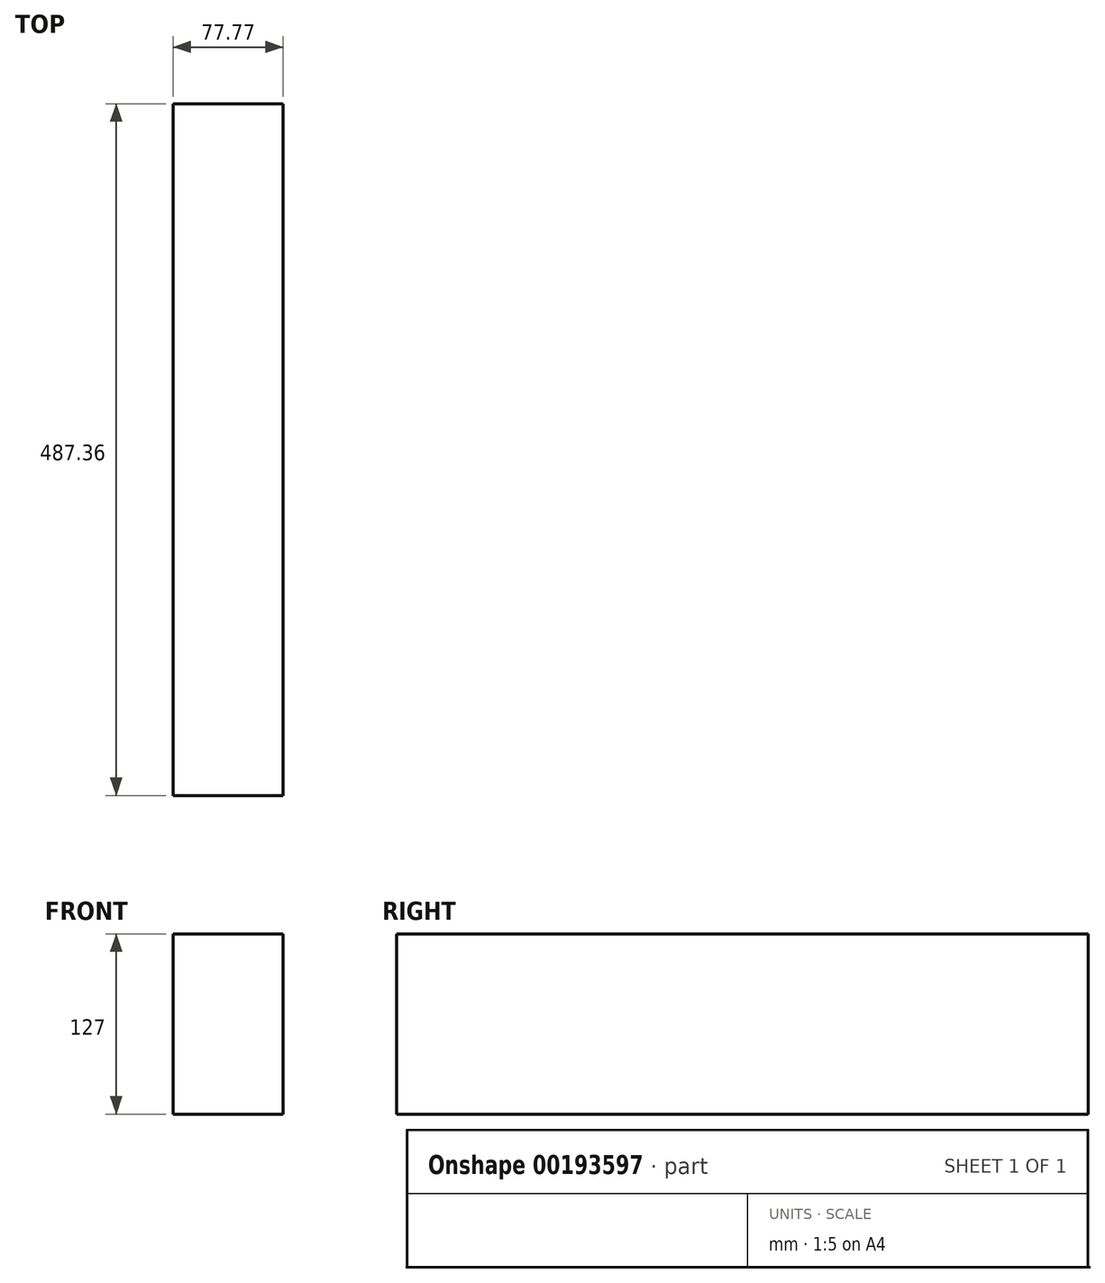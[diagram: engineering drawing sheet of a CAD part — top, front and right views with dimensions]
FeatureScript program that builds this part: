
annotation { "Feature Type Name" : "Feature", "Feature Type Description" : "" }
export const myFeature = defineFeature(function(context is Context, id is Id, definition is map)
    precondition{}
    {
        {
            var Q0;
            Q0=qCreatedBy(makeId("Top.planeOp"),FACE);
            var sketch = newSketch(context, id + "F0", { "sketchPlane" : qUnion([Q0])});
            skLineSegment(sketch, "E0.bottom", {"start": v(0, 0) * mm, "end": v(77.77, 0) * mm});
            skLineSegment(sketch, "E0.top", {"start": v(0, -487.36) * mm, "end": v(77.77, -487.36) * mm});
            skLineSegment(sketch, "E0.left", {"start": v(0, -487.36) * mm, "end": v(0, 0) * mm});
            skLineSegment(sketch, "E0.right", {"start": v(77.77, -487.36) * mm, "end": v(77.77, 0) * mm});
            skSolve(sketch);
        }
        {
            var Q0;
            Q0 = qSketchRegion(id + "F0", true);
            extrude(context, id + "F1", {"entities" : qUnion([Q0]), "oppositeDirection" : true, "depth" : 127 * mm});
        }
    });
